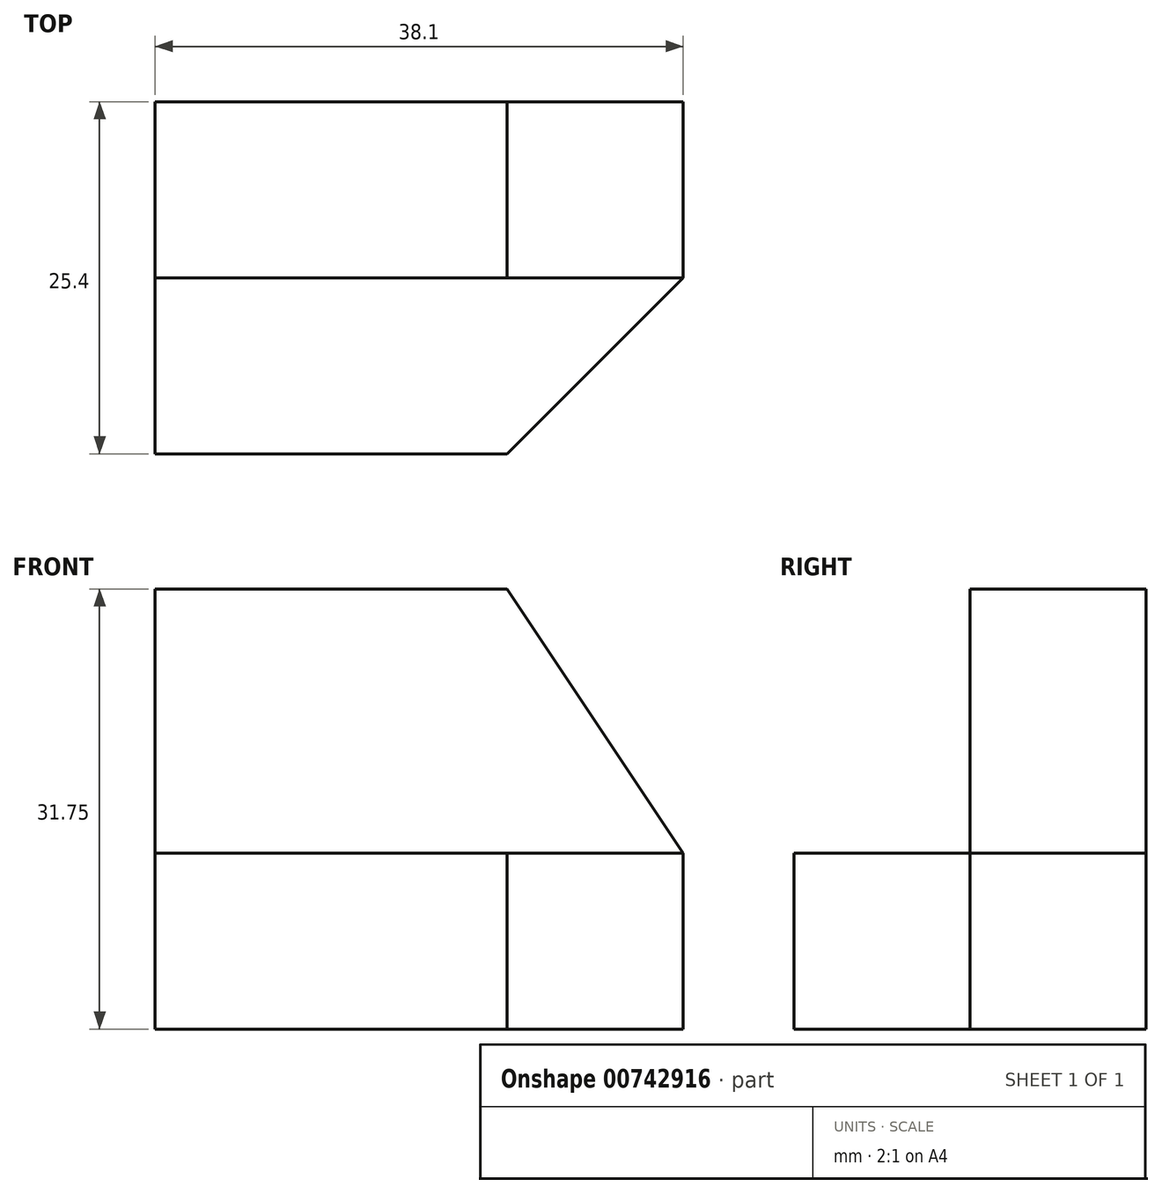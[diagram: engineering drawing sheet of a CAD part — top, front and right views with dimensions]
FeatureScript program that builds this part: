
annotation { "Feature Type Name" : "Feature", "Feature Type Description" : "" }
export const myFeature = defineFeature(function(context is Context, id is Id, definition is map)
    precondition{}
    {
        {
            var Q0;
            Q0=qCreatedBy(makeId("Front.planeOp"),FACE);
            var sketch = newSketch(context, id + "F0", { "sketchPlane" : qUnion([Q0])});
            skLineSegment(sketch, "E0", {"start": v(0, 0) * mm, "end": v(0, 31.75) * mm});
            skLineSegment(sketch, "E1", {"start": v(0, 31.75) * mm, "end": v(25.4, 31.75) * mm});
            skLineSegment(sketch, "E2", {"start": v(25.4, 31.75) * mm, "end": v(38.1, 12.7) * mm});
            skLineSegment(sketch, "E3", {"start": v(38.1, 12.7) * mm, "end": v(38.1, 0) * mm});
            skLineSegment(sketch, "E4", {"start": v(38.1, 0) * mm, "end": v(0, 0) * mm});
            skSolve(sketch);
        }
        {
            var Q0;
            Q0=makeQuery(id+"F0.imprint","IMPRINT",FACE,{"disambiguationData":[TD([[makeQuery(id+"F0.imprint","IMPRINT",EDGE,{"derivedFrom":sQuery(id+"F0.wireOp",EDGE,"E0")}),-1.0]])]});
            extrude(context, id + "F1", {"entities" : qUnion([Q0]), "depth" : 25.4 * mm, "offsetDistance" : 25.4 * mm});
        }
        {
            var Q0;
            Q0=makeQuery(id+"F1.opExtrude","SWEPT_FACE",FACE,{"disambiguationData":[OSD([sQuery(id+"F0.wireOp",EDGE,"E0")])]});
            var sketch = newSketch(context, id + "F2", { "sketchPlane" : qUnion([Q0])});
            skLineSegment(sketch, "E5", {"start": v(12.7, 31.75) * mm, "end": v(12.7, 12.7) * mm});
            skLineSegment(sketch, "E6", {"start": v(12.7, 12.7) * mm, "end": v(25.4, 12.7) * mm});
            skLineSegment(sketch, "E7", {"start": v(25.4, 12.7) * mm, "end": v(25.4, 31.75) * mm});
            skLineSegment(sketch, "E8", {"start": v(25.4, 31.75) * mm, "end": v(12.7, 31.75) * mm});
            skSolve(sketch);
        }
        {
            var Q0;
            Q0=makeQuery(id+"F2.imprint","IMPRINT",FACE,{"disambiguationData":[TD([[makeQuery(id+"F2.imprint","IMPRINT",EDGE,{"derivedFrom":sQuery(id+"F2.wireOp",EDGE,"E5")}),1.0]])]});
            extrude(context, id + "F3", {"entities" : qUnion([Q0]), "operationType" : NewBodyOperationType.REMOVE, "oppositeDirection" : true, "depth" : 38.1 * mm, "offsetDistance" : 25.4 * mm});
        }
        {
            var Q0;
            Q0=makeQuery(id+"F3.boolean.opBoolean","COPY",FACE,{"derivedFrom":makeQuery(id+"F3.opExtrude","SWEPT_FACE",FACE,{"disambiguationData":[OSD([sQuery(id+"F2.wireOp",EDGE,"E6")])]})});
            var sketch = newSketch(context, id + "F4", { "sketchPlane" : qUnion([Q0])});
            skLineSegment(sketch, "E9", {"start": v(38.1, -25.4) * mm, "end": v(25.4, -25.4) * mm});
            skLineSegment(sketch, "E10", {"start": v(25.4, -25.4) * mm, "end": v(38.1, -12.7) * mm});
            skLineSegment(sketch, "E11", {"start": v(38.1, -12.7) * mm, "end": v(38.1, -25.4) * mm});
            skSolve(sketch);
        }
        {
            var Q0;
            Q0=makeQuery(id+"F4.imprint","IMPRINT",FACE,{"disambiguationData":[TD([[makeQuery(id+"F4.imprint","IMPRINT",EDGE,{"derivedFrom":sQuery(id+"F4.wireOp",EDGE,"E9")}),-1.0]])]});
            extrude(context, id + "F5", {"entities" : qUnion([Q0]), "operationType" : NewBodyOperationType.REMOVE, "oppositeDirection" : true, "depth" : 25.4 * mm, "offsetDistance" : 25.4 * mm});
        }
    });
